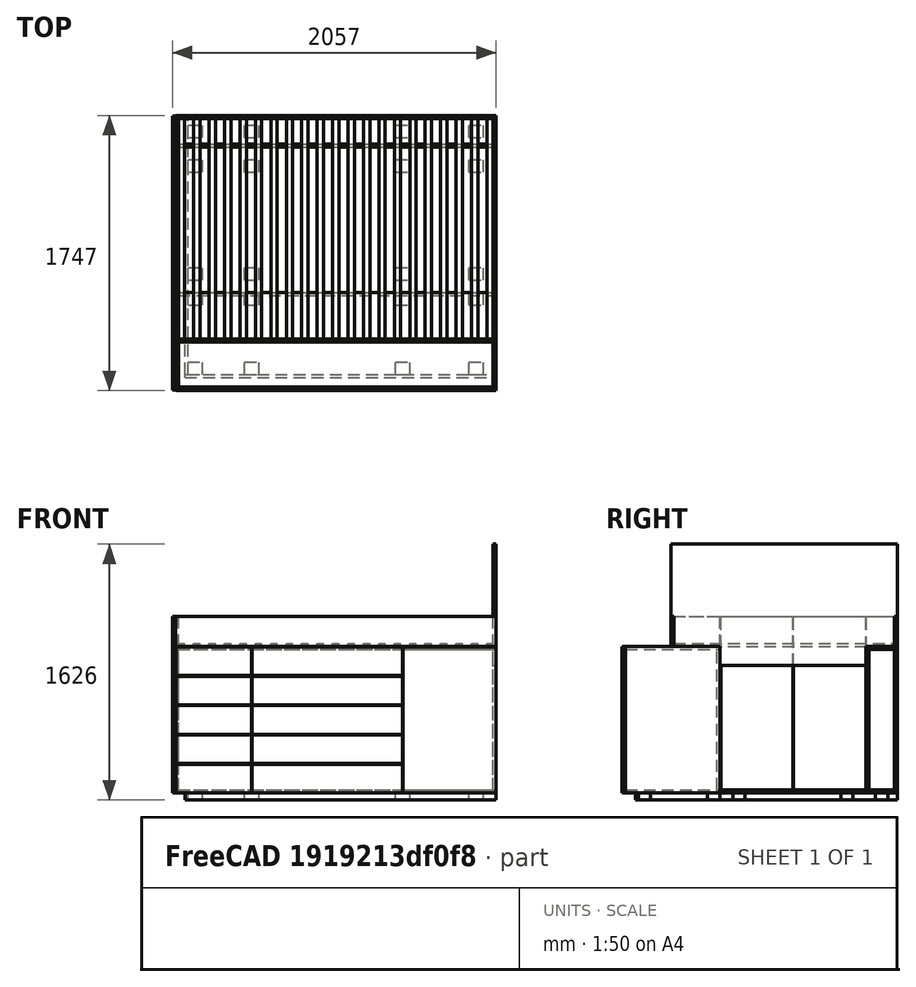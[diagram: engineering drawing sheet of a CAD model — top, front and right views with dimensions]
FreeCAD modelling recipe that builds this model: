
FCSTD DOCUMENT  (FreeCAD 0.21R33771 (Git))
Label: bed001
License: All rights reserved
LicenseURL: https://en.wikipedia.org/wiki/All_rights_reserved
objects: Part::Box×82, App::LinkGroup×6, Part::MultiFuse×2, Part::FeaturePython×1, App::DocumentObjectGroup×1
note: 85 computed .brp shape members not serialized (recipe doc carries the construction recipe); baked Part::Feature solids carry a one-line shape summary decoded from their .brp

FEATURE [Part::Box] Box008  label="Cube008"
  AttacherType = Attacher::AttachEngine3D
  Height = 893
  Length = 2000
  Placement = pos=(19,556,38) rot=(0,0,1;0rad)
  Width = 19
FEATURE [Part::Box] Box009  label="Cube009"
  AttacherType = Attacher::AttachEngine3D
  Height = 19
  Length = 2000
  Placement = pos=(19,-25,931) rot=(0,0,1;0rad)
  Width = 600
FEATURE [Part::Box] Box010  label="Cube010"
  AttacherType = Attacher::AttachEngine3D
  Height = 931
  Length = 19
  Placement = pos=(0,-25,19) rot=(0,0,1;0rad)
  Width = 600
FEATURE [Part::Box] Box011  label="Cube011"
  AttacherType = Attacher::AttachEngine3D
  Height = 931
  Length = 19
  Placement = pos=(2019,-25,19) rot=(0,0,1;0rad)
  Width = 600
FEATURE [Part::Box] Box012  label="Cube012"
  AttacherType = Attacher::AttachEngine3D
  Height = 19
  Length = 2000
  Placement = pos=(19,-25,19) rot=(0,0,1;0rad)
  Width = 600
FEATURE [Part::Box] Box013  label="Cube013"
  AttacherType = Attacher::AttachEngine3D
  Height = 931
  Length = 2038
  Placement = pos=(0,1500,19) rot=(0,0,1;0rad)
  Width = 19
FEATURE [Part::Box] Box014  label="Cube014"
  AttacherType = Attacher::AttachEngine3D
  Height = 931
  Length = 2038
  Placement = pos=(0,1681,19) rot=(0,0,1;0rad)
  Width = 19
FEATURE [Part::Box] Box015  label="Cube015"
  AttacherType = Attacher::AttachEngine3D
  Height = 19
  Length = 2038
  Placement = pos=(0,1519,19) rot=(0,0,1;0rad)
  Width = 162
FEATURE [Part::Box] Box016  label="Cube016"
  AttacherType = Attacher::AttachEngine3D
  Height = 19
  Length = 2038
  Placement = pos=(0,1519,931) rot=(0,0,1;0rad)
  Width = 162
FEATURE [Part::Box] Box017  label="BedLeft"
  AttacherType = Attacher::AttachEngine3D
  Height = 190
  Length = 2038
  Placement = pos=(0,1681,950) rot=(0,0,1;0rad)
  Width = 19
FEATURE [Part::Box] Box018  label="BedRight"
  AttacherType = Attacher::AttachEngine3D
  Height = 190
  Length = 2038
  Placement = pos=(0,262,950) rot=(0,0,1;0rad)
  Width = 19
FEATURE [Part::Box] Box019  label="Floor"
  AttacherType = Attacher::AttachEngine3D
  Height = 19
  Length = 2038
  Placement = pos=(0,575,19) rot=(0,0,1;0rad)
  Width = 925
FEATURE [Part::Box] Box020  label="Cube020"
  AttacherType = Attacher::AttachEngine3D
  Height = 190
  Length = 19
  Placement = pos=(0,281,950) rot=(0,0,1;0rad)
  Width = 1400
FEATURE [Part::Box] Box021  label="Cube021"
  AttacherType = Attacher::AttachEngine3D
  Height = 120
  Length = 19
  Placement = pos=(2019,575,830) rot=(0,0,1;0rad)
  Width = 925
FEATURE [Part::Box] Box023  label="Cube023"
  AttacherType = Attacher::AttachEngine3D
  Height = 190
  Length = 19
  Placement = pos=(2019,281,950) rot=(0,0,1;0rad)
  Width = 1400
FEATURE [Part::Box] Box024  label="Cube024"
  AttacherType = Attacher::AttachEngine3D
  Height = 460
  Length = 19
  Placement = pos=(2019,262,1140) rot=(0,0,1;0rad)
  Width = 1438
FEATURE [Part::MultiFuse] Fusion  label="Headboard"
  Shapes = -> [Box021,Box023,Box024]
FEATURE [Part::Box] Box025  label="Cube025"
  AttacherType = Attacher::AttachEngine3D
  Height = 120
  Length = 19
  Placement = pos=(0,575,830) rot=(0,0,1;0rad)
  Width = 925
FEATURE [Part::MultiFuse] Fusion001  label="Footboard"
  Shapes = -> [Box025,Box020]
FEATURE [Part::Box] Box026  label="Cube026"
  AttacherType = Attacher::AttachEngine3D
  Height = 20
  Length = 40
  Placement = pos=(19,281,950) rot=(0,0,1;0rad)
  Width = 1400
FEATURE [Part::Box] Box027  label="Cube027"
  AttacherType = Attacher::AttachEngine3D
  Height = 20
  Length = 40
  Placement = pos=(1979,281,950) rot=(0,0,1;0rad)
  Width = 1400
FEATURE [Part::Box] Box028  label="Cube028"
  AttacherType = Attacher::AttachEngine3D
  Height = 20
  Length = 40
  Placement = pos=(117,281,950) rot=(0,0,1;0rad)
  Width = 1400
FEATURE [Part::Box] Box029  label="Cube029"
  AttacherType = Attacher::AttachEngine3D
  Height = 20
  Length = 40
  Placement = pos=(215,281,950) rot=(0,0,1;0rad)
  Width = 1400
FEATURE [Part::Box] Box030  label="Cube030"
  AttacherType = Attacher::AttachEngine3D
  Height = 20
  Length = 40
  Placement = pos=(313,281,950) rot=(0,0,1;0rad)
  Width = 1400
FEATURE [Part::Box] Box031  label="Cube031"
  AttacherType = Attacher::AttachEngine3D
  Height = 20
  Length = 40
  Placement = pos=(411,281,950) rot=(0,0,1;0rad)
  Width = 1400
FEATURE [Part::Box] Box032  label="Cube032"
  AttacherType = Attacher::AttachEngine3D
  Height = 20
  Length = 40
  Placement = pos=(509,281,950) rot=(0,0,1;0rad)
  Width = 1400
FEATURE [Part::Box] Box033  label="Cube033"
  AttacherType = Attacher::AttachEngine3D
  Height = 20
  Length = 40
  Placement = pos=(607,281,950) rot=(0,0,1;0rad)
  Width = 1400
FEATURE [Part::Box] Box034  label="Cube034"
  AttacherType = Attacher::AttachEngine3D
  Height = 20
  Length = 40
  Placement = pos=(705,281,950) rot=(0,0,1;0rad)
  Width = 1400
FEATURE [Part::Box] Box035  label="Cube035"
  AttacherType = Attacher::AttachEngine3D
  Height = 20
  Length = 40
  Placement = pos=(803,281,950) rot=(0,0,1;0rad)
  Width = 1400
FEATURE [Part::Box] Box036  label="Cube036"
  AttacherType = Attacher::AttachEngine3D
  Height = 20
  Length = 40
  Placement = pos=(607,281,950) rot=(0,0,1;0rad)
  Width = 1400
FEATURE [Part::Box] Box037  label="Cube037"
  AttacherType = Attacher::AttachEngine3D
  Height = 20
  Length = 40
  Placement = pos=(705,281,950) rot=(0,0,1;0rad)
  Width = 1400
FEATURE [Part::Box] Box038  label="Cube038"
  AttacherType = Attacher::AttachEngine3D
  Height = 20
  Length = 40
  Placement = pos=(803,281,950) rot=(0,0,1;0rad)
  Width = 1400
FEATURE [Part::Box] Box039  label="Cube039"
  AttacherType = Attacher::AttachEngine3D
  Height = 20
  Length = 40
  Placement = pos=(901,281,950) rot=(0,0,1;0rad)
  Width = 1400
FEATURE [Part::Box] Box040  label="Cube040"
  AttacherType = Attacher::AttachEngine3D
  Height = 20
  Length = 40
  Placement = pos=(999,281,950) rot=(0,0,1;0rad)
  Width = 1400
FEATURE [Part::Box] Box041  label="Cube041"
  AttacherType = Attacher::AttachEngine3D
  Height = 20
  Length = 40
  Placement = pos=(1097,281,950) rot=(0,0,1;0rad)
  Width = 1400
FEATURE [Part::Box] Box042  label="Cube042"
  AttacherType = Attacher::AttachEngine3D
  Height = 20
  Length = 40
  Placement = pos=(1195,281,950) rot=(0,0,1;0rad)
  Width = 1400
FEATURE [Part::Box] Box043  label="Cube043"
  AttacherType = Attacher::AttachEngine3D
  Height = 20
  Length = 40
  Placement = pos=(1293,281,950) rot=(0,0,1;0rad)
  Width = 1400
FEATURE [Part::Box] Box044  label="Cube044"
  AttacherType = Attacher::AttachEngine3D
  Height = 20
  Length = 40
  Placement = pos=(1097,281,950) rot=(0,0,1;0rad)
  Width = 1400
FEATURE [Part::Box] Box045  label="Cube045"
  AttacherType = Attacher::AttachEngine3D
  Height = 20
  Length = 40
  Placement = pos=(1195,281,950) rot=(0,0,1;0rad)
  Width = 1400
FEATURE [Part::Box] Box046  label="Cube046"
  AttacherType = Attacher::AttachEngine3D
  Height = 20
  Length = 40
  Placement = pos=(1293,281,950) rot=(0,0,1;0rad)
  Width = 1400
FEATURE [Part::Box] Box047  label="Cube047"
  AttacherType = Attacher::AttachEngine3D
  Height = 20
  Length = 40
  Placement = pos=(1391,281,950) rot=(0,0,1;0rad)
  Width = 1400
FEATURE [Part::Box] Box048  label="Cube048"
  AttacherType = Attacher::AttachEngine3D
  Height = 20
  Length = 40
  Placement = pos=(1489,281,950) rot=(0,0,1;0rad)
  Width = 1400
FEATURE [Part::Box] Box049  label="Cube049"
  AttacherType = Attacher::AttachEngine3D
  Height = 20
  Length = 40
  Placement = pos=(1587,281,950) rot=(0,0,1;0rad)
  Width = 1400
FEATURE [Part::Box] Box050  label="Cube050"
  AttacherType = Attacher::AttachEngine3D
  Height = 20
  Length = 40
  Placement = pos=(1685,281,950) rot=(0,0,1;0rad)
  Width = 1400
FEATURE [Part::Box] Box051  label="Cube051"
  AttacherType = Attacher::AttachEngine3D
  Height = 20
  Length = 40
  Placement = pos=(1783,281,950) rot=(0,0,1;0rad)
  Width = 1400
FEATURE [Part::Box] Box052  label="Cube052"
  AttacherType = Attacher::AttachEngine3D
  Height = 20
  Length = 40
  Placement = pos=(1881,281,950) rot=(0,0,1;0rad)
  Width = 1400
FEATURE [App::LinkGroup] LinkGroup  label="Lattenrost"
  ElementList = -> [Box052,Box026,Box027,Box028,Box029,Box030,Box031,Box032,Box033,Box034,Box035,Box036,Box037,Box038,Box039,Box040,Box041,Box042,Box043,Box044,Box045,Box046,Box047,Box048,Box049,Box050,Box051]
  LinkMode = 0
FEATURE [App::LinkGroup] LinkGroup001  label="RightIsle"
  ElementList = -> [Box009,Box010,Box008,Box011,Box012]
  LinkMode = 0
FEATURE [App::LinkGroup] LinkGroup002  label="LeftIsle"
  ElementList = -> [Box014,Box013,Box015,Box016]
  LinkMode = 0
FEATURE [Part::Box] Box053  label="BlendeR"
  AttacherType = Attacher::AttachEngine3D
  Height = 931
  Length = 19
  Placement = pos=(-19,-45,19) rot=(0,0,1;0rad)
  Width = 620
FEATURE [Part::Box] Box054  label="BlendeR001"
  AttacherType = Attacher::AttachEngine3D
  Height = 190
  Length = 19
  Placement = pos=(-19,262,950) rot=(0,0,1;0rad)
  Width = 313
FEATURE [Part::FeaturePython] Connect  label="BlendeR002"  # WARN: FeaturePython — macro-defined, semantics opaque (R4)
  Objects = -> [Box054,Box053]
  Tolerance = 0
FEATURE [Part::Box] Box055  label="BlendeR003"
  AttacherType = Attacher::AttachEngine3D
  Height = 1121
  Length = 19
  Placement = pos=(-19,579,19) rot=(0,0,1;0rad)
  Width = 458.5
FEATURE [Part::Box] Box056  label="BlendeR004"
  AttacherType = Attacher::AttachEngine3D
  Height = 1121
  Length = 19
  Placement = pos=(-19,1041.5,19) rot=(0,0,1;0rad)
  Width = 458.5
FEATURE [Part::Box] Box057  label="BlendeR005"
  AttacherType = Attacher::AttachEngine3D
  Height = 1121
  Length = 19
  Placement = pos=(-19,1504,19) rot=(0,0,1;0rad)
  Width = 192
FEATURE [Part::Box] Box058  label="SchubFront001"
  AttacherType = Attacher::AttachEngine3D
  Height = 182.28
  Length = 480
  Placement = pos=(3,-47,19) rot=(0,0,1;0rad)
  Width = 19
FEATURE [Part::Box] Box059  label="SchubFront002"
  AttacherType = Attacher::AttachEngine3D
  Height = 182.28
  Length = 480
  Placement = pos=(3,-47,205.28) rot=(0,0,1;0rad)
  Width = 19
FEATURE [Part::Box] Box060  label="SchubFront003"
  AttacherType = Attacher::AttachEngine3D
  Height = 182.28
  Length = 480
  Placement = pos=(3,-47,391.56) rot=(0,0,1;0rad)
  Width = 19
FEATURE [Part::Box] Box061  label="SchubFront004"
  AttacherType = Attacher::AttachEngine3D
  Height = 182.28
  Length = 480
  Placement = pos=(3,-47,577.84) rot=(0,0,1;0rad)
  Width = 19
FEATURE [Part::Box] Box062  label="SchubFront005"
  AttacherType = Attacher::AttachEngine3D
  Height = 182.28
  Length = 480
  Placement = pos=(3,-47,764.12) rot=(0,0,1;0rad)
  Width = 19
FEATURE [Part::Box] Box063  label="SchubFront006"
  AttacherType = Attacher::AttachEngine3D
  Height = 182.28
  Length = 956
  Placement = pos=(487,-47,19) rot=(0,0,1;0rad)
  Width = 19
FEATURE [Part::Box] Box064  label="SchubFront007"
  AttacherType = Attacher::AttachEngine3D
  Height = 182.28
  Length = 956
  Placement = pos=(487,-47,205.28) rot=(0,0,1;0rad)
  Width = 19
FEATURE [Part::Box] Box065  label="SchubFront008"
  AttacherType = Attacher::AttachEngine3D
  Height = 182.28
  Length = 956
  Placement = pos=(487,-47,391.56) rot=(0,0,1;0rad)
  Width = 19
FEATURE [Part::Box] Box066  label="SchubFront009"
  AttacherType = Attacher::AttachEngine3D
  Height = 182.28
  Length = 956
  Placement = pos=(487,-47,577.84) rot=(0,0,1;0rad)
  Width = 19
FEATURE [Part::Box] Box067  label="SchubFront010"
  AttacherType = Attacher::AttachEngine3D
  Height = 182.28
  Length = 956
  Placement = pos=(487,-47,764.12) rot=(0,0,1;0rad)
  Width = 19
FEATURE [Part::Box] Box068  label="Tuer003"
  AttacherType = Attacher::AttachEngine3D
  Height = 927
  Length = 588
  Placement = pos=(1447,-47,19) rot=(0,0,1;0rad)
  Width = 19
FEATURE [Part::Box] Box069  label="SockelFuss001"
  AttacherType = Attacher::AttachEngine3D
  Height = 45
  Length = 92
  Placement = pos=(80,55,-26) rot=(0,0,1;0rad)
  Width = 79
FEATURE [Part::Box] Box070  label="SockelFuss002"
  AttacherType = Attacher::AttachEngine3D
  Height = 45
  Length = 92
  Placement = pos=(80,496,-26) rot=(0,0,1;0rad)
  Width = 79
FEATURE [Part::Box] Box071  label="SockelFuss003"
  AttacherType = Attacher::AttachEngine3D
  Height = 45
  Length = 92
  Placement = pos=(80,1341,-26) rot=(0,0,1;0rad)
  Width = 79
FEATURE [Part::Box] Box072  label="SockelFuss004"
  AttacherType = Attacher::AttachEngine3D
  Height = 45
  Length = 92
  Placement = pos=(80,655,-26) rot=(0,0,1;0rad)
  Width = 79
FEATURE [Part::Box] Box073  label="SockelFuss005"
  AttacherType = Attacher::AttachEngine3D
  Height = 45
  Length = 92
  Placement = pos=(80,1560.5,-26) rot=(0,0,1;0rad)
  Width = 79
FEATURE [Part::Box] Box074  label="SockelFuss006"
  AttacherType = Attacher::AttachEngine3D
  Height = 45
  Length = 92
  Placement = pos=(440.5,1560.5,-26) rot=(0,0,1;0rad)
  Width = 79
FEATURE [Part::Box] Box075  label="SockelFuss007"
  AttacherType = Attacher::AttachEngine3D
  Height = 45
  Length = 92
  Placement = pos=(440.5,55,-26) rot=(0,0,1;0rad)
  Width = 79
FEATURE [Part::Box] Box076  label="SockelFuss008"
  AttacherType = Attacher::AttachEngine3D
  Height = 45
  Length = 92
  Placement = pos=(440.5,496,-26) rot=(0,0,1;0rad)
  Width = 79
FEATURE [Part::Box] Box077  label="SockelFuss009"
  AttacherType = Attacher::AttachEngine3D
  Height = 45
  Length = 92
  Placement = pos=(440.5,1341,-26) rot=(0,0,1;0rad)
  Width = 79
FEATURE [Part::Box] Box078  label="SockelFuss010"
  AttacherType = Attacher::AttachEngine3D
  Height = 45
  Length = 92
  Placement = pos=(440.5,655,-26) rot=(0,0,1;0rad)
  Width = 79
FEATURE [Part::Box] Box079  label="SockelFuss011"
  AttacherType = Attacher::AttachEngine3D
  Height = 45
  Length = 92
  Placement = pos=(1398.5,1560.5,-26) rot=(0,0,1;0rad)
  Width = 79
FEATURE [Part::Box] Box080  label="SockelFuss012"
  AttacherType = Attacher::AttachEngine3D
  Height = 45
  Length = 92
  Placement = pos=(1398.5,55,-26) rot=(0,0,1;0rad)
  Width = 79
FEATURE [Part::Box] Box081  label="SockelFuss013"
  AttacherType = Attacher::AttachEngine3D
  Height = 45
  Length = 92
  Placement = pos=(1398.5,496,-26) rot=(0,0,1;0rad)
  Width = 79
FEATURE [Part::Box] Box082  label="SockelFuss014"
  AttacherType = Attacher::AttachEngine3D
  Height = 45
  Length = 92
  Placement = pos=(1398.5,1341,-26) rot=(0,0,1;0rad)
  Width = 79
FEATURE [Part::Box] Box083  label="SockelFuss015"
  AttacherType = Attacher::AttachEngine3D
  Height = 45
  Length = 92
  Placement = pos=(1398.5,655,-26) rot=(0,0,1;0rad)
  Width = 79
FEATURE [Part::Box] Box084  label="SockelFuss016"
  AttacherType = Attacher::AttachEngine3D
  Height = 45
  Length = 92
  Placement = pos=(1866,655,-26) rot=(0,0,1;0rad)
  Width = 79
FEATURE [Part::Box] Box085  label="SockelFuss017"
  AttacherType = Attacher::AttachEngine3D
  Height = 45
  Length = 92
  Placement = pos=(1866,1341,-26) rot=(0,0,1;0rad)
  Width = 79
FEATURE [Part::Box] Box086  label="SockelFuss018"
  AttacherType = Attacher::AttachEngine3D
  Height = 45
  Length = 92
  Placement = pos=(1866,496,-26) rot=(0,0,1;0rad)
  Width = 79
FEATURE [Part::Box] Box087  label="SockelFuss019"
  AttacherType = Attacher::AttachEngine3D
  Height = 45
  Length = 92
  Placement = pos=(1866,55,-26) rot=(0,0,1;0rad)
  Width = 79
FEATURE [Part::Box] Box088  label="SockelFuss020"
  AttacherType = Attacher::AttachEngine3D
  Height = 45
  Length = 92
  Placement = pos=(1866,1560.5,-26) rot=(0,0,1;0rad)
  Width = 79
FEATURE [Part::Box] Box089  label="SockelLeiste001"
  AttacherType = Attacher::AttachEngine3D
  Height = 45
  Length = 1977
  Placement = pos=(61,36,-26) rot=(0,0,1;0rad)
  Width = 19
FEATURE [Part::Box] Box090  label="SockelLeiste002"
  AttacherType = Attacher::AttachEngine3D
  Height = 45
  Length = 19
  Placement = pos=(61,55,-26) rot=(0,0,1;0rad)
  Width = 1645
FEATURE [App::LinkGroup] LinkGroup004  label="Sockel"
  ElementList = -> [Box069,Box070,Box071,Box072,Box073,Box074,Box075,Box076,Box077,Box078,Box079,Box080,Box081,Box082,Box083,Box084,Box085,Box086,Box087,Box088,Box089,Box090]
  LinkMode = 0
FEATURE [App::LinkGroup] LinkGroup005  label="Fronten"
  ElementList = -> [Connect,Box055,Box056,Box057,Box058,Box059,Box060,Box061,Box062,Box063,Box064,Box065,Box066,Box067,Box068]
  LinkMode = 0
FEATURE [App::LinkGroup] LinkGroup006  label="Frame"
  ElementList = -> [Box017,Box018,Fusion,Fusion001]
  LinkMode = 0
FEATURE [App::DocumentObjectGroup] Draft_Construction  label="Construction"
  Group = -> [Box019,LinkGroup,LinkGroup001,LinkGroup002,LinkGroup004,LinkGroup005,LinkGroup006]
